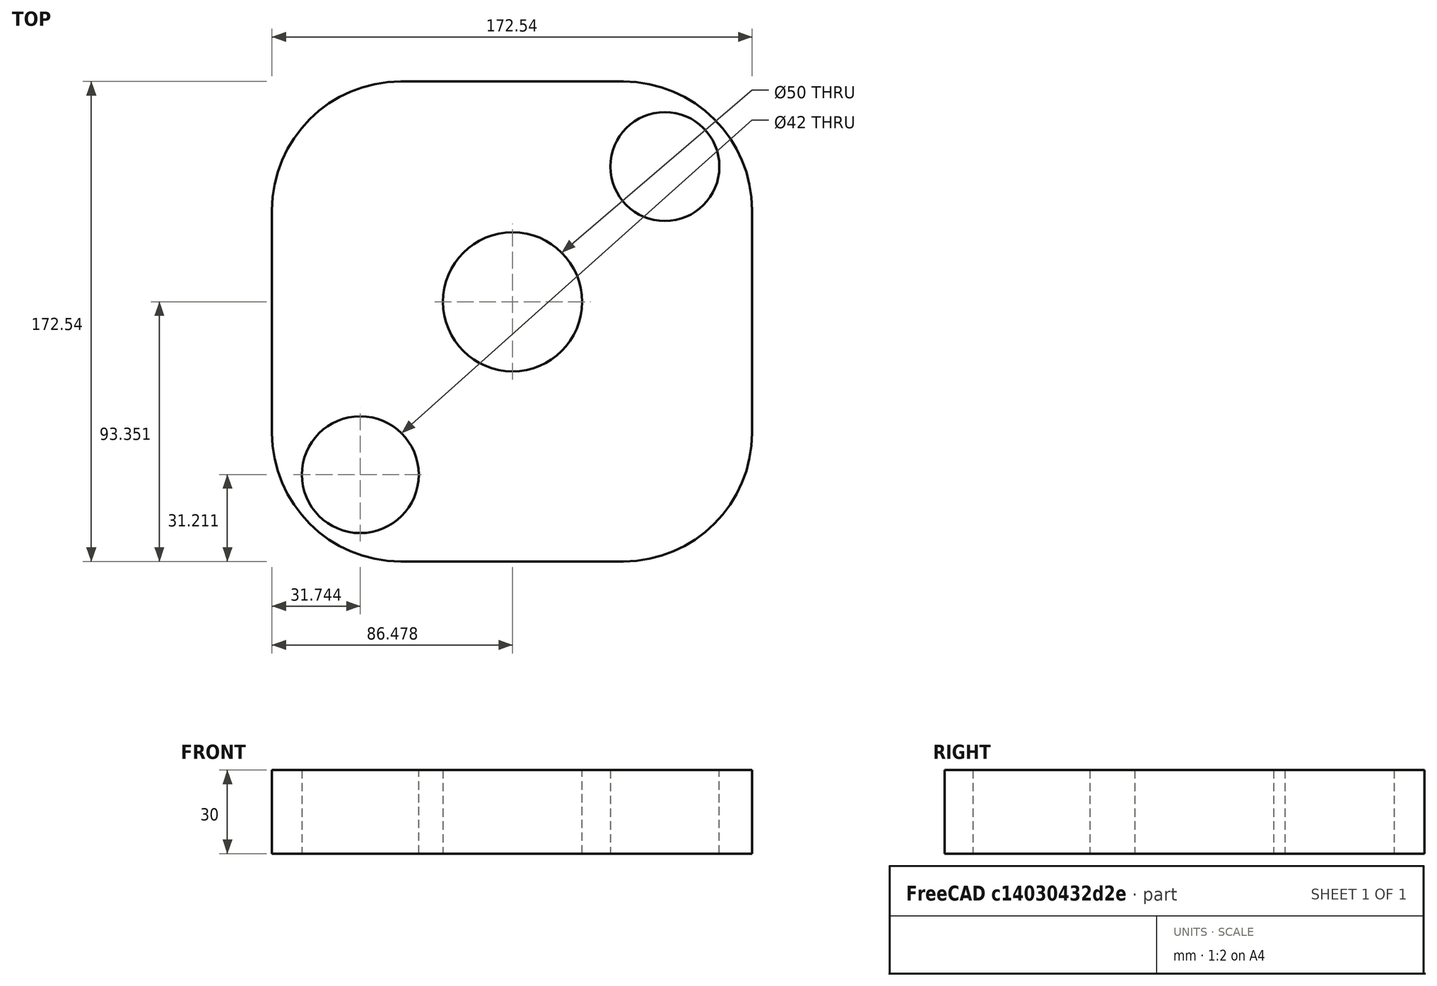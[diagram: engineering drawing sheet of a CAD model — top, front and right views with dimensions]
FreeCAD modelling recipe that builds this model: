
FCSTD DOCUMENT  (FreeCAD 0.18R16131 (Git))
Label: Momentum_Mold_Plate_160X200_12T_25mm(lm12uu)_Base
License: All rights reserved
LicenseURL: http://en.wikipedia.org/wiki/All_rights_reserved
objects: PartDesign::Pad×2, Sketcher::SketchObject×1, PartDesign::Body×1
note: 6 computed .brp shape members not serialized (recipe doc carries the construction recipe); baked Part::Feature solids carry a one-line shape summary decoded from their .brp

FEATURE [Sketcher::SketchObject] Sketch
  MapMode = 5
  Support = -> [XY_Plane]
  sketch-geometry (11):
    g0: LineSegment StartX=-35.5842 StartY=-63.1111 StartZ=0 EndX=44.4158 EndY=-63.1111 EndZ=0
    g1: LineSegment StartX=90.685 StartY=-16.8419 StartZ=0 EndX=90.685 EndY=63.1581 EndZ=0
    g2: LineSegment StartX=44.4158 StartY=109.427 StartZ=0 EndX=-35.5842 EndY=109.427 EndZ=0
    g3: LineSegment StartX=-81.8534 StartY=63.1581 StartZ=0 EndX=-81.8534 EndY=-16.8419 EndZ=0
    g4: Circle CenterX=4.62833 CenterY=30.2412 CenterZ=0 NormalX=0 NormalY=0 NormalZ=1 AngleXU=0 Radius=25
    g5: Circle CenterX=-50.1062 CenterY=-31.8986 CenterZ=0 NormalX=0 NormalY=0 NormalZ=1 AngleXU=0 Radius=21
    g6: Circle CenterX=59.3629 CenterY=78.8583 CenterZ=0 NormalX=0 NormalY=0 NormalZ=1 AngleXU=0 Radius=19.5845
    g7: ArcOfCircle CenterX=-35.5842 CenterY=63.1581 CenterZ=0 NormalX=0 NormalY=0 NormalZ=1 AngleXU=0 Radius=46.2692 StartAngle=1.5708 EndAngle=3.14159
    g8: ArcOfCircle CenterX=44.4158 CenterY=63.1581 CenterZ=0 NormalX=0 NormalY=0 NormalZ=1 AngleXU=0 Radius=46.2692 StartAngle=1e-16 EndAngle=1.5708
    g9: ArcOfCircle CenterX=44.4158 CenterY=-16.8419 CenterZ=0 NormalX=0 NormalY=0 NormalZ=1 AngleXU=0 Radius=46.2692 StartAngle=4.71239 EndAngle=6.28319
    g10: ArcOfCircle CenterX=-35.5842 CenterY=-16.8419 CenterZ=0 NormalX=0 NormalY=0 NormalZ=1 AngleXU=0 Radius=46.2692 StartAngle=3.14159 EndAngle=4.71239
  constraints (19):
    c: Horizontal(g0)
    c: Horizontal(g2)
    c: Vertical(g1)
    c: Vertical(g3)
    c: Radius(g4) = 25
    c: Radius(g5) = 21
    c: Tangent(g2,g7) = -1.5708
    c: Tangent(g3,g7) = -1.5708
    c: Tangent(g2,g8) = -1.5708
    c: Tangent(g1,g8) = -1.5708
    c: Tangent(g1,g9) = -1.5708
    c: Tangent(g0,g9) = -1.5708
    c: Tangent(g0,g10) = -1.5708
    c: Tangent(g3,g10) = -1.5708
    c: Vertical(g7,g10)
    c: DistanceY(g1,g1) = 80
    c: DistanceY(g3,g3) = 80
    c: Horizontal(g1,g3)
    c: DistanceX(g2,g2) = 80
FEATURE [PartDesign::Pad] Pad
  Length = 30
  Length2 = 100
  Profile = -> Sketch
  Type = 0
FEATURE [PartDesign::Pad] Pad001
  BaseFeature = -> Pad
  Length = 30
  Length2 = 100
  Profile = -> Sketch
  Type = 0
FEATURE [PartDesign::Body] Body
  Group = -> [Sketch,Pad,Pad001]
  Origin = -> Origin
  Tip = -> Pad001
